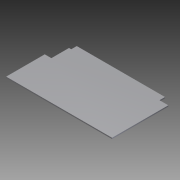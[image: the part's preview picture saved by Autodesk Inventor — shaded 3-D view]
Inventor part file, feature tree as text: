
AUTODESK INVENTOR PART (.ipt)
format: ipt  version: 2012 (Build 160160000, 160)  size: 100,352 bytes
history: native  units: in
note: dims shown in document units (in); Inventor stores cm internally (conversion verified against a paired STEP export)
features: extrude x3, sketch x3
ambient origin geometry x8: Origin, YZ Plane, XZ Plane, XY Plane, X Axis, Y Axis, Z Axis, Center Point
bodies: Solid1 (feature_tree)
feature tree (6):
  extrude  "Extrusion1"  Depth=0.25in
  extrude  "Extrusion2"  Depth=24.0in
  extrude  "Extrusion3"  Depth=0.5in
  sketch  "Sketch1"  dims[d0=25.0in d1=0.25in]
  sketch  "Sketch2"  dims[d2=14.0in d3=0.0in d4=24.0in]
  sketch  "Sketch3"  dims[d5=14.0in d6=0.5in d7=14.0in d8=0.0in d9=2.0in d10=1.25in d11=2.0in d12=1.25in d13=1.5in d14=4.0in d16=1.0in d17=0.0in]
